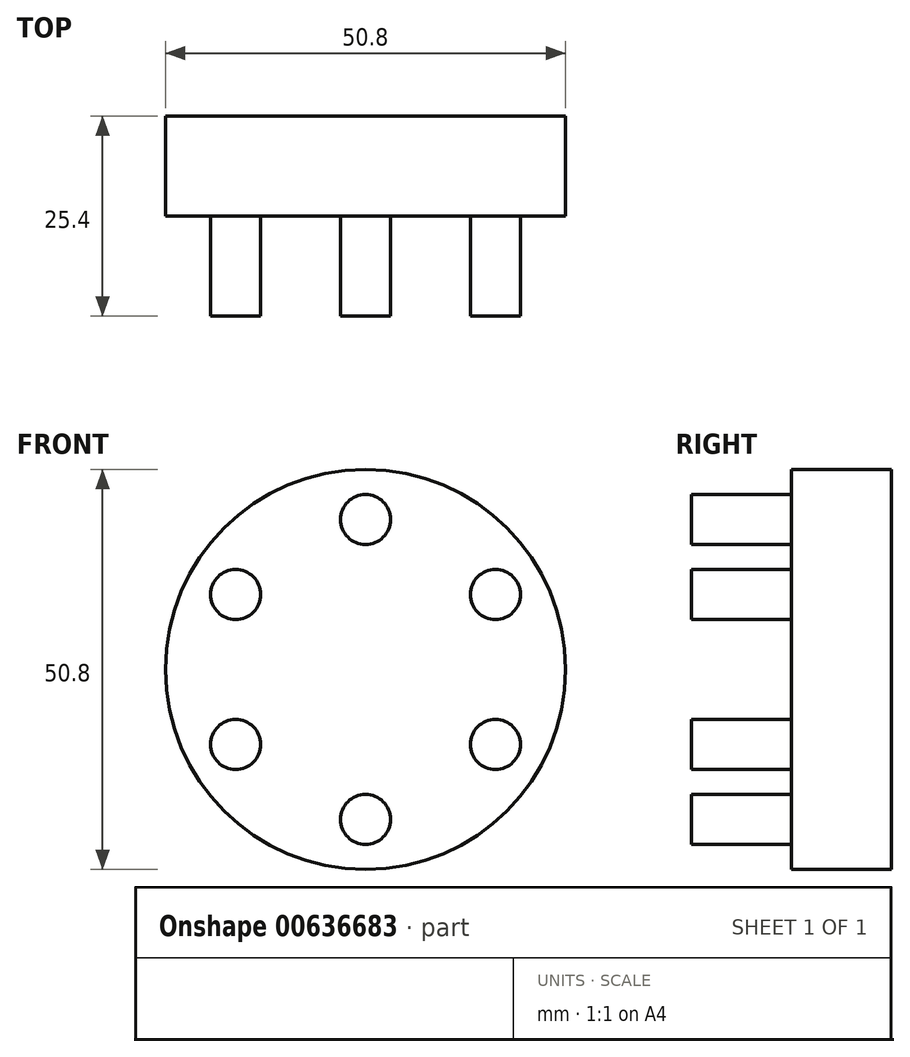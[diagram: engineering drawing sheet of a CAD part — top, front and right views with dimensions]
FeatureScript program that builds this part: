
annotation { "Feature Type Name" : "Feature", "Feature Type Description" : "" }
export const myFeature = defineFeature(function(context is Context, id is Id, definition is map)
    precondition{}
    {
        {
            var Q0;
            Q0=qCreatedBy(makeId("Front.planeOp"),FACE);
            var sketch = newSketch(context, id + "F0", { "sketchPlane" : qUnion([Q0])});
            skCircle(sketch, "E0", {"center": v(0, 0) * mm, "radius": 25.4 * mm});
            skSolve(sketch);
        }
        {
            var Q0;
            Q0 = qSketchRegion(id + "F0", true);
            extrude(context, id + "F1", {"entities" : qUnion([Q0]), "depth" : 12.7 * mm, "offsetDistance" : 25.4 * mm});
        }
        {
            var Q0;
            Q0=makeQuery(id+"F1.opExtrude","CAP_FACE",FACE,{"disambiguationData":[OSD([sQuery(id+"F0.wireOp",EDGE,"E0")])],"isStart":false});
            var sketch = newSketch(context, id + "F2", { "sketchPlane" : qUnion([Q0])});
            skLineSegment(sketch, "E1", {"start": v(0, 25.4) * mm, "end": v(0, 19.05) * mm, "construction": true});
            skCircle(sketch, "E2", {"center": v(0, 19.05) * mm, "radius": 3.18 * mm});
            skCircle(sketch, "E3.1.0", {"center": v(-16.5, 9.53) * mm, "radius": 3.18 * mm});
            skCircle(sketch, "E3.2.0", {"center": v(-16.5, -9.52) * mm, "radius": 3.18 * mm});
            skCircle(sketch, "E3.3.0", {"center": v(0, -19.05) * mm, "radius": 3.18 * mm});
            skCircle(sketch, "E3.4.0", {"center": v(16.5, -9.53) * mm, "radius": 3.18 * mm});
            skCircle(sketch, "E3.5.0", {"center": v(16.5, 9.53) * mm, "radius": 3.18 * mm});
            skPoint(sketch, "E3.center", {"position": v(0, 0) * mm});
            skSolve(sketch);
        }
        {
            var Q0;
            Q0=makeQuery(id+"F2.imprint","IMPRINT",FACE,{"disambiguationData":[TD([[makeQuery(id+"F2.imprint","IMPRINT",EDGE,{"derivedFrom":sQuery(id+"F2.wireOp",EDGE,"E3.1.0")}),1.0]])]});
            var Q1;
            Q1=makeQuery(id+"F2.imprint","IMPRINT",FACE,{"disambiguationData":[TD([[makeQuery(id+"F2.imprint","IMPRINT",EDGE,{"derivedFrom":sQuery(id+"F2.wireOp",EDGE,"E3.2.0")}),1.0]])]});
            var Q2;
            Q2=makeQuery(id+"F2.imprint","IMPRINT",FACE,{"disambiguationData":[TD([[makeQuery(id+"F2.imprint","IMPRINT",EDGE,{"derivedFrom":sQuery(id+"F2.wireOp",EDGE,"E3.3.0")}),1.0]])]});
            var Q3;
            Q3=makeQuery(id+"F2.imprint","IMPRINT",FACE,{"disambiguationData":[TD([[makeQuery(id+"F2.imprint","IMPRINT",EDGE,{"derivedFrom":sQuery(id+"F2.wireOp",EDGE,"E3.4.0")}),1.0]])]});
            var Q4;
            Q4=makeQuery(id+"F2.imprint","IMPRINT",FACE,{"disambiguationData":[TD([[makeQuery(id+"F2.imprint","IMPRINT",EDGE,{"derivedFrom":sQuery(id+"F2.wireOp",EDGE,"E3.5.0")}),1.0]])]});
            var Q5;
            Q5=makeQuery(id+"F2.imprint","IMPRINT",FACE,{"disambiguationData":[TD([[makeQuery(id+"F2.imprint","IMPRINT",EDGE,{"derivedFrom":sQuery(id+"F2.wireOp",EDGE,"E2")}),1.0]])]});
            extrude(context, id + "F3", {"entities" : qUnion([Q0, Q1, Q2, Q3, Q4, Q5]), "operationType" : NewBodyOperationType.ADD, "depth" : 12.7 * mm, "offsetDistance" : 25.4 * mm});
        }
    });
